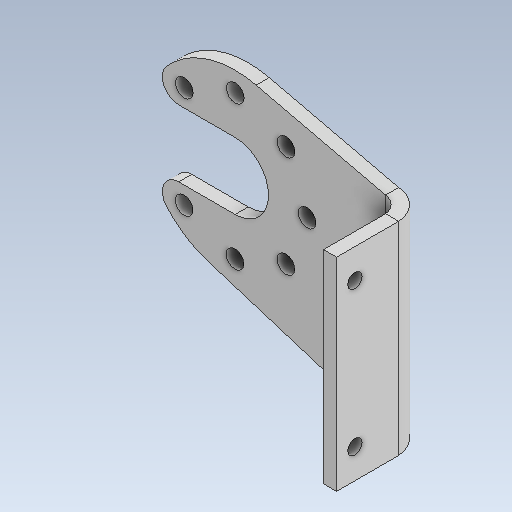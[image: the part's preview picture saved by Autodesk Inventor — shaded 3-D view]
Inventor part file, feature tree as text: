
AUTODESK INVENTOR PART (.ipt)
format: ipt  version: 2020 (Build 240168000, 168)  size: 194,048 bytes
history: native  units: mm
features: other x4, sketch x3, extrude x2, fillet x1
ambient origin geometry x8: Origin, YZ Plane, XZ Plane, XY Plane, X Axis, Y Axis, Z Axis, Center Point
bodies: Body1 (feature_tree)
feature tree (10):
  other  "솔리드1"
  extrude  "돌출1"  Depth=10.2mm
  other  "플랜지1"
  extrude  "돌출2"  Depth=2.0mm TaperAngle=0.0deg
  fillet  "모깎기2"  Radius=2.0mm
  sketch  "스케치1"
  sketch  "스케치2"
  other  "절곡부1"
  other  "구석1"
  sketch  "스케치3"
